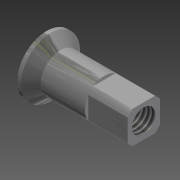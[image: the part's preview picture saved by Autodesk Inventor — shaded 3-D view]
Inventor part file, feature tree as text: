
AUTODESK INVENTOR PART (.ipt)
format: ipt  version: 2015 (Build 190159000, 159)  size: 186,880 bytes
history: native  units: mm
features: sketch x4, extrude x2, chamfer x2, other x1, revolve x1, hole x1, thread x1, projected_geometry x1
ambient origin geometry x8: Origin, YZ Plane, XZ Plane, XY Plane, X Axis, Y Axis, Z Axis, Center Point
bodies: Body1 (feature_tree)
feature tree (13):
  other  "Bryła1"
  revolve  "Obrót1"
  extrude  "Wyciągnięcie proste2"  Depth=11.0mm
  hole  "Otwór1"  [1 undecoded]
  chamfer  "Faza1"  Distance=10.0mm
  chamfer  "Faza2"  Distance=2.5mm
  extrude  "Wyciągnięcie proste3"  TaperAngle=45.0deg  [1 undecoded]
  thread  "Gwint1"
  sketch  "Szkic1"
  sketch  "Szkic2"
  sketch  "Szkic3"
  projected_geometry  "Pętla rzutowana1"
  sketch  "Szkic5"
note: 2 required parameter values undecoded (feature->parameter linkage not recoverable at this tier; creation-order binding heuristic only, values carry confidence <= 0.55)
